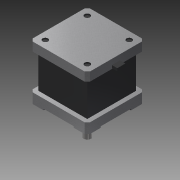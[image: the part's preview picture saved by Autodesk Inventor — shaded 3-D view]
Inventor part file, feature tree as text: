
AUTODESK INVENTOR PART (.ipt)
format: ipt  version: 2014 SP1 (Build 180222100, 222)  size: 235,520 bytes
history: native  units: mm
features: extrude x7, sketch x5, fillet x1, chamfer x1, plane x1, mirror x1, projected_geometry x1
ambient origin geometry x8: Origin, YZ Plane, XZ Plane, XY Plane, X Axis, Y Axis, Z Axis, Center Point
bodies: Solid1 (feature_tree)
feature tree (17):
  extrude  "Extrusion1"  Depth=42.3mm
  sketch  "Sketch2"  dims[d2=39.0mm d3=0.0mm d4=4.0mm]
  extrude  "Extrusion2"  Depth=4.0mm
  extrude  "Extrusion3"  Depth=4.0mm
  extrude  "Extrusion4"  Depth=10.0mm
  fillet  "Fillet1"  Radius=10.0mm
  chamfer  "Chamfer1"  Distance=10.0mm
  extrude  "Extrusion5"  Depth=10.0mm
  plane  "Work Plane1"
  mirror  "Mirror1"
  extrude  "Extrusion6"  Depth=10.0mm
  extrude  "Extrusion8"  Depth=10.0mm
  sketch  "Sketch1"  dims[d0=42.3mm d1=42.3mm]
  sketch  "Sketch3"  dims[d5=4.0mm d6=31.0mm]
  sketch  "Sketch4"  dims[d7=31.0mm d8=10.0mm d9=10.0mm]
  sketch  "Sketch6"  dims[d10=10.0mm d11=10.0mm d12=10.0mm d13=10.0mm d14=10.0mm d15=10.0mm d16=1.0mm d17=0.0mm d18=2.0mm d19=0.0mm d20=22.0mm d21=1.0mm d22=0.0mm d23=3.0mm d24=2.0mm d25=2.0mm d26=45.0deg d27=5.0mm d28=22.0mm d29=0.0mm d30=-19.5mm d31=2.0mm d32=6.0mm d33=4.0mm d34=4.0mm d35=0.0mm d43=3.0mm d44=40.0mm d46=360.0deg d48=26.0mm d49=0.0mm]
  projected_geometry  "Project Cut Edges2"
